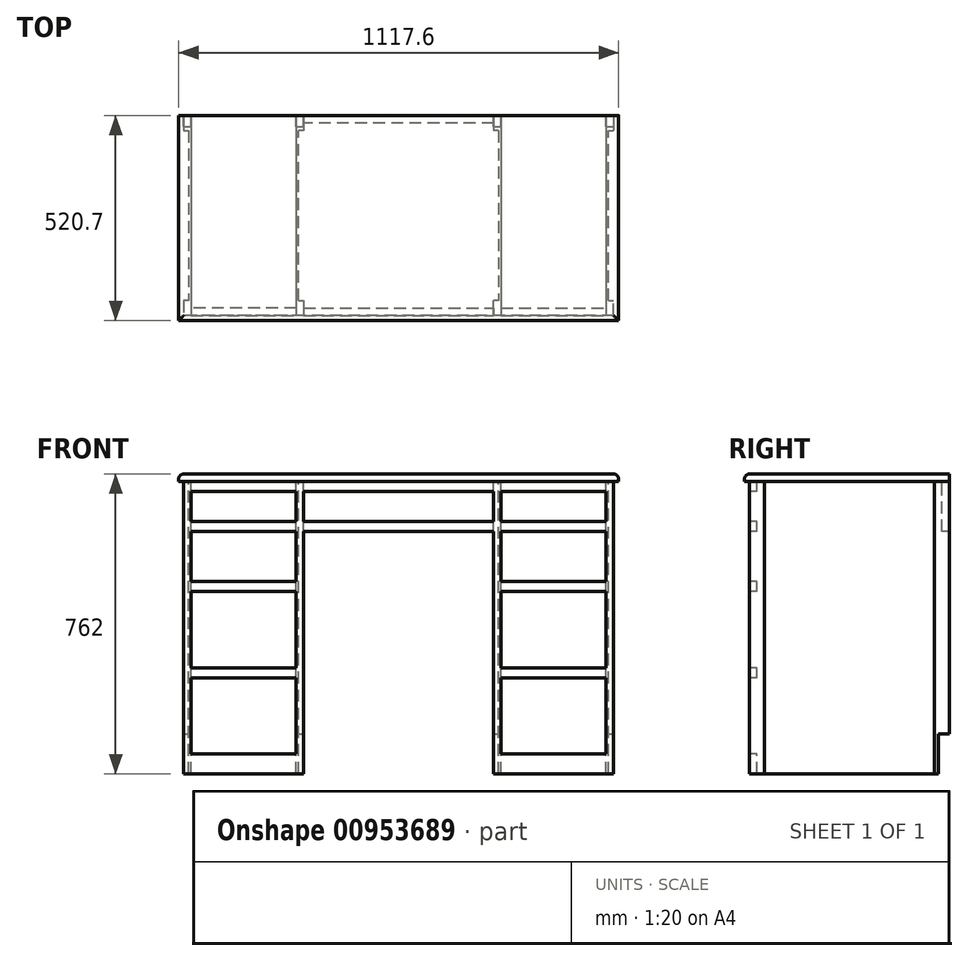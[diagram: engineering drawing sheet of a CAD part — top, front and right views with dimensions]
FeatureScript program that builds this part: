
annotation { "Feature Type Name" : "Feature", "Feature Type Description" : "" }
export const myFeature = defineFeature(function(context is Context, id is Id, definition is map)
    precondition{}
    {
        {
            var Q0;
            Q0=qCreatedBy(makeId("Top.planeOp"),FACE);
            var sketch = newSketch(context, id + "F0", { "sketchPlane" : qUnion([Q0])});
            skLineSegment(sketch, "E0.bottom", {"start": v(-521.2, 263.5) * mm, "end": v(-254.5, 263.5) * mm});
            skLineSegment(sketch, "E0.top", {"start": v(-521.2, -244.5) * mm, "end": v(-254.5, -244.5) * mm});
            skLineSegment(sketch, "E0.left", {"start": v(-521.2, 263.5) * mm, "end": v(-521.2, -244.5) * mm});
            skLineSegment(sketch, "E0.right", {"start": v(-254.5, 263.5) * mm, "end": v(-254.5, -244.5) * mm});
            skLineSegment(sketch, "E1.bottom", {"start": v(266.2, 263.5) * mm, "end": v(532.9, 263.5) * mm});
            skLineSegment(sketch, "E1.top", {"start": v(266.2, -244.5) * mm, "end": v(532.9, -244.5) * mm});
            skLineSegment(sketch, "E1.left", {"start": v(266.2, 263.5) * mm, "end": v(266.2, -244.5) * mm});
            skLineSegment(sketch, "E1.right", {"start": v(532.9, 263.5) * mm, "end": v(532.9, -244.5) * mm});
            skLineSegment(sketch, "E2.bottom", {"start": v(-521.2, -206.4) * mm, "end": v(-540.25, -206.4) * mm});
            skLineSegment(sketch, "E2.top", {"start": v(-521.2, -244.5) * mm, "end": v(-540.25, -244.5) * mm});
            skLineSegment(sketch, "E2.left", {"start": v(-521.2, -206.4) * mm, "end": v(-521.2, -244.5) * mm});
            skLineSegment(sketch, "E2.right", {"start": v(-540.25, -206.4) * mm, "end": v(-540.25, -244.5) * mm});
            skLineSegment(sketch, "E3.bottom", {"start": v(-254.5, -206.4) * mm, "end": v(-235.45, -206.4) * mm});
            skLineSegment(sketch, "E3.top", {"start": v(-254.5, -244.5) * mm, "end": v(-235.45, -244.5) * mm});
            skLineSegment(sketch, "E3.left", {"start": v(-254.5, -206.4) * mm, "end": v(-254.5, -244.5) * mm});
            skLineSegment(sketch, "E3.right", {"start": v(-235.45, -206.4) * mm, "end": v(-235.45, -244.5) * mm});
            skLineSegment(sketch, "E4.bottom", {"start": v(-540.25, 263.5) * mm, "end": v(-521.2, 263.5) * mm});
            skLineSegment(sketch, "E4.top", {"start": v(-540.25, 225.4) * mm, "end": v(-521.2, 225.4) * mm});
            skLineSegment(sketch, "E4.left", {"start": v(-540.25, 263.5) * mm, "end": v(-540.25, 225.4) * mm});
            skLineSegment(sketch, "E4.right", {"start": v(-521.2, 263.5) * mm, "end": v(-521.2, 225.4) * mm});
            skLineSegment(sketch, "E5.bottom", {"start": v(-235.45, 263.5) * mm, "end": v(-254.5, 263.5) * mm});
            skLineSegment(sketch, "E5.top", {"start": v(-235.45, 225.4) * mm, "end": v(-254.5, 225.4) * mm});
            skLineSegment(sketch, "E5.left", {"start": v(-235.45, 263.5) * mm, "end": v(-235.45, 225.4) * mm});
            skLineSegment(sketch, "E5.right", {"start": v(-254.5, 263.5) * mm, "end": v(-254.5, 225.4) * mm});
            skLineSegment(sketch, "E6.bottom", {"start": v(266.2, -244.5) * mm, "end": v(247.15, -244.5) * mm});
            skLineSegment(sketch, "E6.top", {"start": v(266.2, -206.4) * mm, "end": v(247.15, -206.4) * mm});
            skLineSegment(sketch, "E6.left", {"start": v(266.2, -244.5) * mm, "end": v(266.2, -206.4) * mm});
            skLineSegment(sketch, "E6.right", {"start": v(247.15, -244.5) * mm, "end": v(247.15, -206.4) * mm});
            skLineSegment(sketch, "E7.bottom", {"start": v(266.2, 263.5) * mm, "end": v(247.15, 263.5) * mm});
            skLineSegment(sketch, "E7.top", {"start": v(266.2, 225.4) * mm, "end": v(247.15, 225.4) * mm});
            skLineSegment(sketch, "E7.left", {"start": v(266.2, 263.5) * mm, "end": v(266.2, 225.4) * mm});
            skLineSegment(sketch, "E7.right", {"start": v(247.15, 263.5) * mm, "end": v(247.15, 225.4) * mm});
            skLineSegment(sketch, "E8.bottom", {"start": v(532.9, -244.5) * mm, "end": v(551.95, -244.5) * mm});
            skLineSegment(sketch, "E8.top", {"start": v(532.9, -206.4) * mm, "end": v(551.95, -206.4) * mm});
            skLineSegment(sketch, "E8.left", {"start": v(532.9, -244.5) * mm, "end": v(532.9, -206.4) * mm});
            skLineSegment(sketch, "E8.right", {"start": v(551.95, -244.5) * mm, "end": v(551.95, -206.4) * mm});
            skLineSegment(sketch, "E9.bottom", {"start": v(532.9, 263.5) * mm, "end": v(551.95, 263.5) * mm});
            skLineSegment(sketch, "E9.top", {"start": v(532.9, 225.4) * mm, "end": v(551.95, 225.4) * mm});
            skLineSegment(sketch, "E9.left", {"start": v(532.9, 263.5) * mm, "end": v(532.9, 225.4) * mm});
            skLineSegment(sketch, "E9.right", {"start": v(551.95, 263.5) * mm, "end": v(551.95, 225.4) * mm});
            skLineSegment(sketch, "E10", {"start": v(-254.5, 244.44) * mm, "end": v(-521.2, 244.44) * mm});
            skLineSegment(sketch, "E11", {"start": v(266.2, 244.44) * mm, "end": v(532.9, 244.44) * mm});
            skLineSegment(sketch, "E12", {"start": v(266.2, -225.46) * mm, "end": v(532.9, -225.46) * mm});
            skLineSegment(sketch, "E13", {"start": v(-254.5, -225.46) * mm, "end": v(-521.2, -225.46) * mm});
            skLineSegment(sketch, "E14", {"start": v(-527.55, 225.4) * mm, "end": v(-527.55, -206.4) * mm});
            skLineSegment(sketch, "E15", {"start": v(-248.15, -206.4) * mm, "end": v(-248.15, 225.4) * mm});
            skLineSegment(sketch, "E16", {"start": v(259.85, 225.4) * mm, "end": v(259.85, -206.4) * mm});
            skPoint(sketch, "E16.endSnap0", {"position": v(256.67, -206.4) * mm});
            skLineSegment(sketch, "E17", {"start": v(539.25, -206.4) * mm, "end": v(539.25, 225.4) * mm});
            skLineSegment(sketch, "E18.bottom", {"start": v(-552.95, -257.2) * mm, "end": v(564.65, -257.2) * mm});
            skLineSegment(sketch, "E18.top", {"start": v(-552.95, 263.5) * mm, "end": v(564.65, 263.5) * mm});
            skLineSegment(sketch, "E18.left", {"start": v(-552.95, -257.2) * mm, "end": v(-552.95, 263.5) * mm});
            skLineSegment(sketch, "E18.right", {"start": v(564.65, -257.2) * mm, "end": v(564.65, 263.5) * mm});
            skLineSegment(sketch, "E19", {"start": v(247.15, 244.44) * mm, "end": v(-235.45, 244.44) * mm});
            skLineSegment(sketch, "E20", {"start": v(-235.45, -225.46) * mm, "end": v(247.15, -225.46) * mm});
            skLineSegment(sketch, "E21", {"start": v(-235.45, -244.5) * mm, "end": v(247.15, -244.5) * mm});
            skSolve(sketch);
        }
        {
            var Q0;
            {var subQ2=sQuery(id+"F0.wireOp",EDGE,"E11");Q0=makeQuery(id+"F0.imprint","IMPRINT",FACE,{"disambiguationData":[TD([[makeQuery(id+"F0.imprint","IMPRINT",EDGE,{"derivedFrom":subQ2}),-1.0]])]});}
            var Q1;
            {var subQ1=sQuery(id+"F0.wireOp",EDGE,"E7.bottom");Q1=makeQuery(id+"F0.imprint","IMPRINT",FACE,{"disambiguationData":[TD([[makeQuery(id+"F0.imprint","IMPRINT",EDGE,{"derivedFrom":subQ1}),1.0]])]});}
            var Q2;
            {var subQ0=sQuery(id+"F0.wireOp",EDGE,"E1.bottom");Q2=makeQuery(id+"F0.imprint","IMPRINT",FACE,{"disambiguationData":[TD([[makeQuery(id+"F0.imprint","IMPRINT",EDGE,{"derivedFrom":subQ0}),-1.0]])]});}
            var Q3;
            {var subQ1=sQuery(id+"F0.wireOp",EDGE,"E9.bottom");Q3=makeQuery(id+"F0.imprint","IMPRINT",FACE,{"disambiguationData":[TD([[makeQuery(id+"F0.imprint","IMPRINT",EDGE,{"derivedFrom":subQ1}),-1.0]])]});}
            var Q4;
            {var subQ5=sQuery(id+"F0.wireOp",EDGE,"E16");Q4=makeQuery(id+"F0.imprint","IMPRINT",FACE,{"disambiguationData":[TD([[makeQuery(id+"F0.imprint","IMPRINT",EDGE,{"derivedFrom":subQ5}),1.0]])]});}
            var Q5;
            {var subQ5=sQuery(id+"F0.wireOp",EDGE,"E17");Q5=makeQuery(id+"F0.imprint","IMPRINT",FACE,{"disambiguationData":[TD([[makeQuery(id+"F0.imprint","IMPRINT",EDGE,{"derivedFrom":subQ5}),1.0]])]});}
            var Q6;
            {var subQ0=sQuery(id+"F0.wireOp",EDGE,"E0.bottom");Q6=makeQuery(id+"F0.imprint","IMPRINT",FACE,{"disambiguationData":[TD([[makeQuery(id+"F0.imprint","IMPRINT",EDGE,{"derivedFrom":subQ0}),-1.0]])]});}
            var Q7;
            {var subQ5=sQuery(id+"F0.wireOp",EDGE,"E5.bottom");Q7=makeQuery(id+"F0.imprint","IMPRINT",FACE,{"disambiguationData":[TD([[makeQuery(id+"F0.imprint","IMPRINT",EDGE,{"derivedFrom":subQ5}),1.0]])]});}
            var Q8;
            {var subQ0=sQuery(id+"F0.wireOp",EDGE,"E0.top");Q8=makeQuery(id+"F0.imprint","IMPRINT",FACE,{"disambiguationData":[TD([[makeQuery(id+"F0.imprint","IMPRINT",EDGE,{"derivedFrom":subQ0}),1.0]])]});}
            var Q9;
            {var subQ0=sQuery(id+"F0.wireOp",EDGE,"E1.top");Q9=makeQuery(id+"F0.imprint","IMPRINT",FACE,{"disambiguationData":[TD([[makeQuery(id+"F0.imprint","IMPRINT",EDGE,{"derivedFrom":subQ0}),1.0]])]});}
            var Q10;
            {var subQ4=sQuery(id+"F0.wireOp",EDGE,"E2.top");Q10=makeQuery(id+"F0.imprint","IMPRINT",FACE,{"disambiguationData":[TD([[makeQuery(id+"F0.imprint","IMPRINT",EDGE,{"derivedFrom":subQ4}),-1.0]])]});}
            var Q11;
            {var subQ7=sQuery(id+"F0.wireOp",EDGE,"E3.top");Q11=makeQuery(id+"F0.imprint","IMPRINT",FACE,{"disambiguationData":[TD([[makeQuery(id+"F0.imprint","IMPRINT",EDGE,{"derivedFrom":subQ7}),1.0]])]});}
            var Q12;
            {var subQ0=sQuery(id+"F0.wireOp",EDGE,"E6.bottom");Q12=makeQuery(id+"F0.imprint","IMPRINT",FACE,{"disambiguationData":[TD([[makeQuery(id+"F0.imprint","IMPRINT",EDGE,{"derivedFrom":subQ0}),-1.0]])]});}
            var Q13;
            {var subQ3=sQuery(id+"F0.wireOp",EDGE,"E8.bottom");Q13=makeQuery(id+"F0.imprint","IMPRINT",FACE,{"disambiguationData":[TD([[makeQuery(id+"F0.imprint","IMPRINT",EDGE,{"derivedFrom":subQ3}),1.0]])]});}
            var Q14;
            {var subQ5=sQuery(id+"F0.wireOp",EDGE,"E4.bottom");Q14=makeQuery(id+"F0.imprint","IMPRINT",FACE,{"disambiguationData":[TD([[makeQuery(id+"F0.imprint","IMPRINT",EDGE,{"derivedFrom":subQ5}),-1.0]])]});}
            var Q15;
            {var subQ5=sQuery(id+"F0.wireOp",EDGE,"E14");Q15=makeQuery(id+"F0.imprint","IMPRINT",FACE,{"disambiguationData":[TD([[makeQuery(id+"F0.imprint","IMPRINT",EDGE,{"derivedFrom":subQ5}),1.0]])]});}
            var Q16;
            Q16=makeQuery(id+"F0.imprint","IMPRINT",FACE,{"disambiguationData":[TD([[makeQuery(id+"F0.imprint","IMPRINT",EDGE,{"derivedFrom":sQuery(id+"F0.wireOp",EDGE,"E1.bottom")}),1.0]])]});
            var Q17;
            {var subQ5=sQuery(id+"F0.wireOp",EDGE,"E15");Q17=makeQuery(id+"F0.imprint","IMPRINT",FACE,{"disambiguationData":[TD([[makeQuery(id+"F0.imprint","IMPRINT",EDGE,{"derivedFrom":subQ5}),1.0]])]});}
            var Q18;
            {var subQ2=sQuery(id+"F0.wireOp",EDGE,"E10");Q18=makeQuery(id+"F0.imprint","IMPRINT",FACE,{"disambiguationData":[TD([[makeQuery(id+"F0.imprint","IMPRINT",EDGE,{"derivedFrom":subQ2}),1.0]])]});}
            var Q19;
            {var subQ0=sQuery(id+"F0.wireOp",EDGE,"E0.bottom");Q19=makeQuery(id+"F0.imprint","IMPRINT",FACE,{"disambiguationData":[TD([[makeQuery(id+"F0.imprint","IMPRINT",EDGE,{"derivedFrom":subQ0}),-1.0]])]});}
            var Q20;
            {var subQ0=sQuery(id+"F0.wireOp",EDGE,"E5.bottom");Q20=makeQuery(id+"F0.imprint","IMPRINT",FACE,{"disambiguationData":[TD([[makeQuery(id+"F0.imprint","IMPRINT",EDGE,{"derivedFrom":subQ0}),1.0]])]});}
            var Q21;
            {var subQ3=sQuery(id+"F0.wireOp",EDGE,"E4.bottom");Q21=makeQuery(id+"F0.imprint","IMPRINT",FACE,{"disambiguationData":[TD([[makeQuery(id+"F0.imprint","IMPRINT",EDGE,{"derivedFrom":subQ3}),-1.0]])]});}
            var Q22;
            {var subQ0=sQuery(id+"F0.wireOp",EDGE,"E1.bottom");Q22=makeQuery(id+"F0.imprint","IMPRINT",FACE,{"disambiguationData":[TD([[makeQuery(id+"F0.imprint","IMPRINT",EDGE,{"derivedFrom":subQ0}),-1.0]])]});}
            var Q23;
            {var subQ3=sQuery(id+"F0.wireOp",EDGE,"E9.bottom");Q23=makeQuery(id+"F0.imprint","IMPRINT",FACE,{"disambiguationData":[TD([[makeQuery(id+"F0.imprint","IMPRINT",EDGE,{"derivedFrom":subQ3}),-1.0]])]});}
            var Q24;
            Q24=makeQuery(id+"F0.imprint","IMPRINT",FACE,{"disambiguationData":[TD([[makeQuery(id+"F0.imprint","IMPRINT",EDGE,{"derivedFrom":sQuery(id+"F0.wireOp",EDGE,"E0.top")}),-1.0]])]});
            var Q25;
            {var subQ4=sQuery(id+"F0.wireOp",EDGE,"E7.bottom");Q25=makeQuery(id+"F0.imprint","IMPRINT",FACE,{"disambiguationData":[TD([[makeQuery(id+"F0.imprint","IMPRINT",EDGE,{"derivedFrom":subQ4}),1.0]])]});}
            var Q26;
            {var subQ3=sQuery(id+"F0.wireOp",EDGE,"E19");Q26=makeQuery(id+"F0.imprint","IMPRINT",FACE,{"disambiguationData":[TD([[makeQuery(id+"F0.imprint","IMPRINT",EDGE,{"derivedFrom":subQ3}),-1.0]])]});}
            var Q27;
            {var subQ9=sQuery(id+"F0.wireOp",EDGE,"E15");Q27=makeQuery(id+"F0.imprint","IMPRINT",FACE,{"disambiguationData":[TD([[makeQuery(id+"F0.imprint","IMPRINT",EDGE,{"derivedFrom":subQ9}),-1.0]])]});}
            var Q28;
            {var subQ2=sQuery(id+"F0.wireOp",EDGE,"E20");Q28=makeQuery(id+"F0.imprint","IMPRINT",FACE,{"disambiguationData":[TD([[makeQuery(id+"F0.imprint","IMPRINT",EDGE,{"derivedFrom":subQ2}),-1.0]])]});}
            extrude(context, id + "F1", {"entities" : qUnion([Q0, Q1, Q2, Q3, Q4, Q5, Q6, Q7, Q8, Q9, Q10, Q11, Q12, Q13, Q14, Q15, Q16, Q17, Q18, Q19, Q20, Q21, Q22, Q23, Q24, Q25, Q26, Q27, Q28]), "depth" : 19.05 * mm, "offsetDistance" : 25.4 * mm});
        }
        {
            var Q0;
            {var subQ7=sQuery(id+"F0.wireOp",EDGE,"E3.top");Q0=makeQuery(id+"F0.imprint","IMPRINT",FACE,{"disambiguationData":[TD([[makeQuery(id+"F0.imprint","IMPRINT",EDGE,{"derivedFrom":subQ7}),1.0]])]});}
            var Q1;
            {var subQ4=sQuery(id+"F0.wireOp",EDGE,"E2.top");Q1=makeQuery(id+"F0.imprint","IMPRINT",FACE,{"disambiguationData":[TD([[makeQuery(id+"F0.imprint","IMPRINT",EDGE,{"derivedFrom":subQ4}),-1.0]])]});}
            var Q2;
            {var subQ5=sQuery(id+"F0.wireOp",EDGE,"E14");Q2=makeQuery(id+"F0.imprint","IMPRINT",FACE,{"disambiguationData":[TD([[makeQuery(id+"F0.imprint","IMPRINT",EDGE,{"derivedFrom":subQ5}),1.0]])]});}
            var Q3;
            {var subQ5=sQuery(id+"F0.wireOp",EDGE,"E15");Q3=makeQuery(id+"F0.imprint","IMPRINT",FACE,{"disambiguationData":[TD([[makeQuery(id+"F0.imprint","IMPRINT",EDGE,{"derivedFrom":subQ5}),1.0]])]});}
            var Q4;
            {var subQ3=sQuery(id+"F0.wireOp",EDGE,"E4.bottom");Q4=makeQuery(id+"F0.imprint","IMPRINT",FACE,{"disambiguationData":[TD([[makeQuery(id+"F0.imprint","IMPRINT",EDGE,{"derivedFrom":subQ3}),-1.0]])]});}
            var Q5;
            {var subQ0=sQuery(id+"F0.wireOp",EDGE,"E5.bottom");Q5=makeQuery(id+"F0.imprint","IMPRINT",FACE,{"disambiguationData":[TD([[makeQuery(id+"F0.imprint","IMPRINT",EDGE,{"derivedFrom":subQ0}),1.0]])]});}
            var Q6;
            {var subQ4=sQuery(id+"F0.wireOp",EDGE,"E7.bottom");Q6=makeQuery(id+"F0.imprint","IMPRINT",FACE,{"disambiguationData":[TD([[makeQuery(id+"F0.imprint","IMPRINT",EDGE,{"derivedFrom":subQ4}),1.0]])]});}
            var Q7;
            {var subQ3=sQuery(id+"F0.wireOp",EDGE,"E9.bottom");Q7=makeQuery(id+"F0.imprint","IMPRINT",FACE,{"disambiguationData":[TD([[makeQuery(id+"F0.imprint","IMPRINT",EDGE,{"derivedFrom":subQ3}),-1.0]])]});}
            var Q8;
            {var subQ0=sQuery(id+"F0.wireOp",EDGE,"E6.bottom");Q8=makeQuery(id+"F0.imprint","IMPRINT",FACE,{"disambiguationData":[TD([[makeQuery(id+"F0.imprint","IMPRINT",EDGE,{"derivedFrom":subQ0}),-1.0]])]});}
            var Q9;
            {var subQ3=sQuery(id+"F0.wireOp",EDGE,"E8.bottom");Q9=makeQuery(id+"F0.imprint","IMPRINT",FACE,{"disambiguationData":[TD([[makeQuery(id+"F0.imprint","IMPRINT",EDGE,{"derivedFrom":subQ3}),1.0]])]});}
            var Q10;
            {var subQ5=sQuery(id+"F0.wireOp",EDGE,"E17");Q10=makeQuery(id+"F0.imprint","IMPRINT",FACE,{"disambiguationData":[TD([[makeQuery(id+"F0.imprint","IMPRINT",EDGE,{"derivedFrom":subQ5}),1.0]])]});}
            var Q11;
            {var subQ5=sQuery(id+"F0.wireOp",EDGE,"E16");Q11=makeQuery(id+"F0.imprint","IMPRINT",FACE,{"disambiguationData":[TD([[makeQuery(id+"F0.imprint","IMPRINT",EDGE,{"derivedFrom":subQ5}),1.0]])]});}
            extrude(context, id + "F2", {"entities" : qUnion([Q0, Q1, Q2, Q3, Q4, Q5, Q6, Q7, Q8, Q9, Q10, Q11]), "operationType" : NewBodyOperationType.ADD, "oppositeDirection" : true, "depth" : 742.95 * mm, "offsetDistance" : 25.4 * mm});
        }
        {
            var Q0;
            Q0=makeQuery(id+"F1.opExtrude","CAP_EDGE",EDGE,{"disambiguationData":[OSD([sQuery(id+"F0.wireOp",EDGE,"E18.left")])],"isStart":false});
            var Q1;
            Q1=makeQuery(id+"F1.opExtrude","CAP_EDGE",EDGE,{"disambiguationData":[OSD([sQuery(id+"F0.wireOp",EDGE,"E18.bottom")])],"isStart":false});
            var Q2;
            Q2=makeQuery(id+"F1.opExtrude","CAP_EDGE",EDGE,{"disambiguationData":[OSD([sQuery(id+"F0.wireOp",EDGE,"E18.right")])],"isStart":false});
            fillet(context, id + "F3", {"entities" : qUnion([Q0, Q1, Q2]), "radius" : 12.7 * mm, "tangentPropagation" : true, "allowEdgeOverflow" : false});
        }
        {
            var Q0;
            {var subQ3=sQuery(id+"F0.wireOp",EDGE,"E19");Q0=makeQuery(id+"F0.imprint","IMPRINT",FACE,{"disambiguationData":[TD([[makeQuery(id+"F0.imprint","IMPRINT",EDGE,{"derivedFrom":subQ3}),-1.0]])]});}
            extrude(context, id + "F4", {"entities" : qUnion([Q0]), "operationType" : NewBodyOperationType.ADD, "oppositeDirection" : true, "depth" : 127 * mm, "offsetDistance" : 25.4 * mm});
        }
        {
            var Q0;
            {var subQ2=sQuery(id+"F0.wireOp",EDGE,"E20");Q0=makeQuery(id+"F0.imprint","IMPRINT",FACE,{"disambiguationData":[TD([[makeQuery(id+"F0.imprint","IMPRINT",EDGE,{"derivedFrom":subQ2}),-1.0]])]});}
            extrude(context, id + "F5", {"entities" : qUnion([Q0]), "operationType" : NewBodyOperationType.ADD, "oppositeDirection" : true, "depth" : 127 * mm, "offsetDistance" : 25.4 * mm});
        }
        {
            var Q0;
            {var subQ0=sQuery(id+"F0.wireOp",EDGE,"E0.top");Q0=makeQuery(id+"F0.imprint","IMPRINT",FACE,{"disambiguationData":[TD([[makeQuery(id+"F0.imprint","IMPRINT",EDGE,{"derivedFrom":subQ0}),1.0]])]});}
            var Q1;
            {var subQ0=sQuery(id+"F0.wireOp",EDGE,"E1.top");Q1=makeQuery(id+"F0.imprint","IMPRINT",FACE,{"disambiguationData":[TD([[makeQuery(id+"F0.imprint","IMPRINT",EDGE,{"derivedFrom":subQ0}),1.0]])]});}
            var Q2;
            Q2=makeQuery(id+"F2.opExtrude","CAP_FACE",FACE,{"disambiguationData":[OSD([sQuery(id+"F0.wireOp",EDGE,"E0.left"),sQuery(id+"F0.wireOp",EDGE,"E2.bottom"),sQuery(id+"F0.wireOp",EDGE,"E2.top"),sQuery(id+"F0.wireOp",EDGE,"E2.right"),sQuery(id+"F0.wireOp",EDGE,"E4.bottom"),sQuery(id+"F0.wireOp",EDGE,"E4.top"),sQuery(id+"F0.wireOp",EDGE,"E4.left"),sQuery(id+"F0.wireOp",EDGE,"E14")])],"isStart":false});
            extrude(context, id + "F6", {"entities" : qUnion([Q0, Q1]), "operationType" : NewBodyOperationType.ADD, "endBound" : BoundingType.UP_TO_SURFACE, "oppositeDirection" : true, "depth" : 25.4 * mm, "endBoundEntityFace" : qUnion([Q2]), "offsetDistance" : 25.4 * mm});
        }
        {
            var Q0;
            Q0=makeQuery(id+"F6.boolean.opBoolean","MERGE",FACE,{"derivedFrom":[makeQuery(id+"F2.opExtrude","SWEPT_FACE",FACE,{"disambiguationData":[OSD([sQuery(id+"F0.wireOp",EDGE,"E2.top")])]}),makeQuery(id+"F2.opExtrude","SWEPT_FACE",FACE,{"disambiguationData":[OSD([sQuery(id+"F0.wireOp",EDGE,"E8.bottom")])]}),makeQuery(id+"F5.boolean.opBoolean","MERGE",FACE,{"derivedFrom":[makeQuery(id+"F2.opExtrude","SWEPT_FACE",FACE,{"disambiguationData":[OSD([sQuery(id+"F0.wireOp",EDGE,"E3.top")])]}),makeQuery(id+"F2.opExtrude","SWEPT_FACE",FACE,{"disambiguationData":[OSD([sQuery(id+"F0.wireOp",EDGE,"E6.bottom")])]}),makeQuery(id+"F5.opExtrude","SWEPT_FACE",FACE,{"disambiguationData":[OSD([sQuery(id+"F0.wireOp",EDGE,"E21")])]})]}),makeQuery(id+"F6.opExtrude","SWEPT_FACE",FACE,{"disambiguationData":[OSD([sQuery(id+"F0.wireOp",EDGE,"E0.top")])]}),makeQuery(id+"F6.opExtrude","SWEPT_FACE",FACE,{"disambiguationData":[OSD([sQuery(id+"F0.wireOp",EDGE,"E1.top")])]})]});
            var sketch = newSketch(context, id + "F7", { "sketchPlane" : qUnion([Q0])});
            skLineSegment(sketch, "E22.bottom", {"start": v(-235.45, -25.4) * mm, "end": v(247.15, -25.4) * mm});
            skLineSegment(sketch, "E22.top", {"start": v(-235.45, -101.6) * mm, "end": v(247.15, -101.6) * mm});
            skLineSegment(sketch, "E22.left", {"start": v(-235.45, -25.4) * mm, "end": v(-235.45, -101.6) * mm});
            skLineSegment(sketch, "E22.right", {"start": v(247.15, -25.4) * mm, "end": v(247.15, -101.6) * mm});
            skLineSegment(sketch, "E23.bottom", {"start": v(-521.2, -25.4) * mm, "end": v(-254.5, -25.4) * mm});
            skLineSegment(sketch, "E23.top", {"start": v(-521.2, -101.6) * mm, "end": v(-254.5, -101.6) * mm});
            skLineSegment(sketch, "E23.left", {"start": v(-521.2, -25.4) * mm, "end": v(-521.2, -101.6) * mm});
            skLineSegment(sketch, "E23.right", {"start": v(-254.5, -25.4) * mm, "end": v(-254.5, -101.6) * mm});
            skLineSegment(sketch, "E24.bottom", {"start": v(-521.2, -127) * mm, "end": v(-254.5, -127) * mm});
            skLineSegment(sketch, "E24.top", {"start": v(-521.2, -254) * mm, "end": v(-254.5, -254) * mm});
            skLineSegment(sketch, "E24.left", {"start": v(-521.2, -127) * mm, "end": v(-521.2, -254) * mm});
            skLineSegment(sketch, "E24.right", {"start": v(-254.5, -127) * mm, "end": v(-254.5, -254) * mm});
            skLineSegment(sketch, "E25.bottom", {"start": v(266.2, -25.4) * mm, "end": v(532.9, -25.4) * mm});
            skLineSegment(sketch, "E25.top", {"start": v(266.2, -101.6) * mm, "end": v(532.9, -101.6) * mm});
            skLineSegment(sketch, "E25.left", {"start": v(266.2, -25.4) * mm, "end": v(266.2, -101.6) * mm});
            skLineSegment(sketch, "E25.right", {"start": v(532.9, -25.4) * mm, "end": v(532.9, -101.6) * mm});
            skPoint(sketch, "E26.firstSnap0", {"position": v(5.85, -127) * mm});
            skLineSegment(sketch, "E26.bottom", {"start": v(266.2, -127) * mm, "end": v(532.9, -127) * mm});
            skLineSegment(sketch, "E26.top", {"start": v(266.2, -254) * mm, "end": v(532.9, -254) * mm});
            skLineSegment(sketch, "E26.left", {"start": v(266.2, -127) * mm, "end": v(266.2, -254) * mm});
            skLineSegment(sketch, "E26.right", {"start": v(532.9, -127) * mm, "end": v(532.9, -254) * mm});
            skLineSegment(sketch, "E27.bottom", {"start": v(266.2, -279.4) * mm, "end": v(532.9, -279.4) * mm});
            skLineSegment(sketch, "E27.top", {"start": v(266.2, -473.08) * mm, "end": v(532.9, -473.08) * mm});
            skLineSegment(sketch, "E27.left", {"start": v(266.2, -279.4) * mm, "end": v(266.2, -473.08) * mm});
            skLineSegment(sketch, "E27.right", {"start": v(532.9, -279.4) * mm, "end": v(532.9, -473.08) * mm});
            skLineSegment(sketch, "E28.bottom", {"start": v(266.2, -498.48) * mm, "end": v(532.9, -498.48) * mm});
            skLineSegment(sketch, "E28.top", {"start": v(266.2, -692.15) * mm, "end": v(532.9, -692.15) * mm});
            skLineSegment(sketch, "E28.left", {"start": v(266.2, -498.48) * mm, "end": v(266.2, -692.15) * mm});
            skLineSegment(sketch, "E28.right", {"start": v(532.9, -498.48) * mm, "end": v(532.9, -692.15) * mm});
            skLineSegment(sketch, "E29.bottom", {"start": v(-521.2, -279.4) * mm, "end": v(-254.5, -279.4) * mm});
            skLineSegment(sketch, "E29.top", {"start": v(-521.2, -473.08) * mm, "end": v(-254.5, -473.07) * mm});
            skLineSegment(sketch, "E29.left", {"start": v(-521.2, -279.4) * mm, "end": v(-521.2, -473.08) * mm});
            skLineSegment(sketch, "E29.right", {"start": v(-254.5, -279.4) * mm, "end": v(-254.5, -473.08) * mm});
            skLineSegment(sketch, "E30.bottom", {"start": v(-521.2, -498.48) * mm, "end": v(-254.5, -498.47) * mm});
            skLineSegment(sketch, "E30.top", {"start": v(-521.2, -692.15) * mm, "end": v(-254.5, -692.15) * mm});
            skLineSegment(sketch, "E30.left", {"start": v(-521.2, -498.48) * mm, "end": v(-521.2, -692.15) * mm});
            skLineSegment(sketch, "E30.right", {"start": v(-254.5, -498.47) * mm, "end": v(-254.5, -692.15) * mm});
            skSolve(sketch);
        }
        {
            var Q0;
            Q0=makeQuery(id+"F7.imprint","IMPRINT",FACE,{"disambiguationData":[TD([[makeQuery(id+"F7.imprint","IMPRINT",EDGE,{"derivedFrom":sQuery(id+"F7.wireOp",EDGE,"E22.bottom")}),-1.0]])]});
            var Q1;
            Q1=makeQuery(id+"F7.imprint","IMPRINT",FACE,{"disambiguationData":[TD([[makeQuery(id+"F7.imprint","IMPRINT",EDGE,{"derivedFrom":sQuery(id+"F7.wireOp",EDGE,"E29.bottom")}),-1.0]])]});
            var Q2;
            Q2=makeQuery(id+"F7.imprint","IMPRINT",FACE,{"disambiguationData":[TD([[makeQuery(id+"F7.imprint","IMPRINT",EDGE,{"derivedFrom":sQuery(id+"F7.wireOp",EDGE,"E24.bottom")}),-1.0]])]});
            var Q3;
            Q3=makeQuery(id+"F7.imprint","IMPRINT",FACE,{"disambiguationData":[TD([[makeQuery(id+"F7.imprint","IMPRINT",EDGE,{"derivedFrom":sQuery(id+"F7.wireOp",EDGE,"E23.bottom")}),-1.0]])]});
            var Q4;
            Q4=makeQuery(id+"F7.imprint","IMPRINT",FACE,{"disambiguationData":[TD([[makeQuery(id+"F7.imprint","IMPRINT",EDGE,{"derivedFrom":sQuery(id+"F7.wireOp",EDGE,"E30.bottom")}),-1.0]])]});
            var Q5;
            Q5=makeQuery(id+"F7.imprint","IMPRINT",FACE,{"disambiguationData":[TD([[makeQuery(id+"F7.imprint","IMPRINT",EDGE,{"derivedFrom":sQuery(id+"F7.wireOp",EDGE,"E28.bottom")}),-1.0]])]});
            var Q6;
            Q6=makeQuery(id+"F7.imprint","IMPRINT",FACE,{"disambiguationData":[TD([[makeQuery(id+"F7.imprint","IMPRINT",EDGE,{"derivedFrom":sQuery(id+"F7.wireOp",EDGE,"E27.bottom")}),-1.0]])]});
            var Q7;
            Q7=makeQuery(id+"F7.imprint","IMPRINT",FACE,{"disambiguationData":[TD([[makeQuery(id+"F7.imprint","IMPRINT",EDGE,{"derivedFrom":sQuery(id+"F7.wireOp",EDGE,"E26.bottom")}),-1.0]])]});
            var Q8;
            Q8=makeQuery(id+"F7.imprint","IMPRINT",FACE,{"disambiguationData":[TD([[makeQuery(id+"F7.imprint","IMPRINT",EDGE,{"derivedFrom":sQuery(id+"F7.wireOp",EDGE,"E25.bottom")}),-1.0]])]});
            extrude(context, id + "F8", {"entities" : qUnion([Q0, Q1, Q2, Q3, Q4, Q5, Q6, Q7, Q8]), "operationType" : NewBodyOperationType.REMOVE, "oppositeDirection" : true, "depth" : 25.4 * mm, "offsetDistance" : 25.4 * mm});
        }
        {
            var Q0;
            Q0=makeQuery(id+"F2.opExtrude","SWEPT_FACE",FACE,{"disambiguationData":[OSD([sQuery(id+"F0.wireOp",EDGE,"E9.right")])]});
            var sketch = newSketch(context, id + "F9", { "sketchPlane" : qUnion([Q0])});
            skLineSegment(sketch, "E31.bottom", {"start": v(263.5, -742.95) * mm, "end": v(234.92, -742.95) * mm});
            skLineSegment(sketch, "E31.top", {"start": v(263.5, -641.35) * mm, "end": v(234.92, -641.35) * mm});
            skLineSegment(sketch, "E31.left", {"start": v(263.5, -742.95) * mm, "end": v(263.5, -641.35) * mm});
            skLineSegment(sketch, "E31.right", {"start": v(234.92, -742.95) * mm, "end": v(234.92, -641.35) * mm});
            skSolve(sketch);
        }
        {
            var Q0;
            Q0=makeQuery(id+"F9.imprint","IMPRINT",FACE,{"disambiguationData":[TD([[makeQuery(id+"F9.imprint","IMPRINT",EDGE,{"derivedFrom":sQuery(id+"F9.wireOp",EDGE,"E31.bottom")}),-1.0]])]});
            extrude(context, id + "F10", {"entities" : qUnion([Q0]), "operationType" : NewBodyOperationType.REMOVE, "endBound" : BoundingType.THROUGH_ALL, "oppositeDirection" : true, "depth" : 25.4 * mm, "offsetDistance" : 25.4 * mm});
        }
    });
